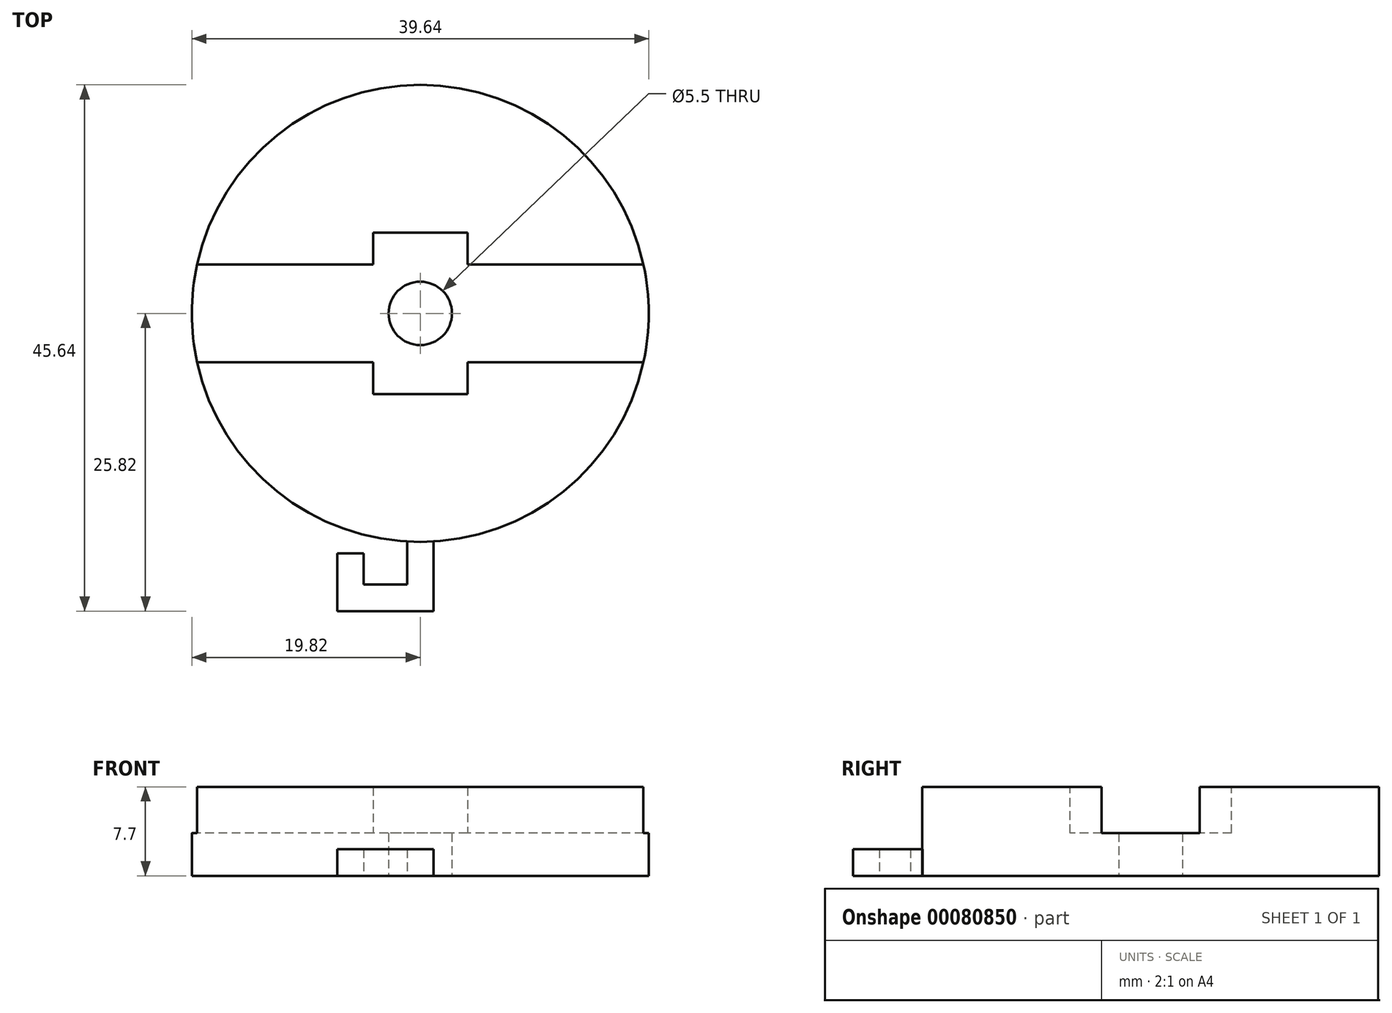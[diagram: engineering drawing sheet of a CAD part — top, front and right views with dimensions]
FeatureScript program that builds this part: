
annotation { "Feature Type Name" : "Feature", "Feature Type Description" : "" }
export const myFeature = defineFeature(function(context is Context, id is Id, definition is map)
    precondition{}
    {
        {
            var Q0;
            Q0=qCreatedBy(makeId("Top.planeOp"),FACE);
            var sketch = newSketch(context, id + "F0", { "sketchPlane" : qUnion([Q0])});
            skCircle(sketch, "E0", {"center": v(0, 0) * mm, "radius": 19.82 * mm});
            skSolve(sketch);
        }
        {
            var Q0;
            Q0 = qSketchRegion(id + "F0", true);
            extrude(context, id + "F1", {"entities" : qUnion([Q0]), "depth" : 7.7 * mm});
        }
        {
            var Q0;
            Q0=makeQuery(id+"F1.opExtrude","CAP_FACE",FACE,{"disambiguationData":[OSD([sQuery(id+"F0.wireOp",EDGE,"E0")])],"isStart":false});
            var sketch = newSketch(context, id + "F2", { "sketchPlane" : qUnion([Q0])});
            skLineSegment(sketch, "E1.bottom", {"start": v(4.1, 7) * mm, "end": v(-4.1, 7) * mm});
            skLineSegment(sketch, "E1.top", {"start": v(4.1, -7) * mm, "end": v(-4.1, -7) * mm});
            skLineSegment(sketch, "E1.left", {"start": v(4.1, 7) * mm, "end": v(4.1, -7) * mm});
            skLineSegment(sketch, "E1.right", {"start": v(-4.1, 7) * mm, "end": v(-4.1, -7) * mm});
            skPoint(sketch, "E1.middle", {"position": v(0, 0) * mm});
            skSolve(sketch);
        }
        {
            var Q0;
            Q0 = qSketchRegion(id + "F2", true);
            extrude(context, id + "F3", {"entities" : qUnion([Q0]), "operationType" : NewBodyOperationType.REMOVE, "oppositeDirection" : true, "depth" : 4 * mm});
        }
        {
            var Q0;
            Q0=makeQuery(id+"F1.opExtrude","CAP_FACE",FACE,{"disambiguationData":[OSD([sQuery(id+"F0.wireOp",EDGE,"E0")])],"isStart":false});
            var sketch = newSketch(context, id + "F4", { "sketchPlane" : qUnion([Q0])});
            skLineSegment(sketch, "E2.bottom", {"start": v(20.32, -4.25) * mm, "end": v(-20.32, -4.25) * mm});
            skLineSegment(sketch, "E2.top", {"start": v(20.32, 4.25) * mm, "end": v(-20.32, 4.25) * mm});
            skLineSegment(sketch, "E2.left", {"start": v(20.32, -4.25) * mm, "end": v(20.32, 4.25) * mm});
            skLineSegment(sketch, "E2.right", {"start": v(-20.32, -4.25) * mm, "end": v(-20.32, 4.25) * mm});
            skPoint(sketch, "E2.middle", {"position": v(0, 0) * mm});
            skSolve(sketch);
        }
        {
            var Q0;
            Q0 = qSketchRegion(id + "F4", true);
            extrude(context, id + "F5", {"entities" : qUnion([Q0]), "operationType" : NewBodyOperationType.REMOVE, "oppositeDirection" : true, "depth" : 4 * mm});
        }
        {
            var Q0;
            Q0=makeQuery(id+"F1.opExtrude","CAP_FACE",FACE,{"disambiguationData":[OSD([sQuery(id+"F0.wireOp",EDGE,"E0")])],"isStart":true});
            var sketch = newSketch(context, id + "F6", { "sketchPlane" : qUnion([Q0])});
            skLineSegment(sketch, "E3.bottom", {"start": v(1.15, 25.82) * mm, "end": v(-1.15, 25.82) * mm});
            skLineSegment(sketch, "E3.left", {"start": v(1.15, 19.82) * mm, "end": v(1.15, 25.82) * mm});
            skLineSegment(sketch, "E3.right", {"start": v(-1.15, 19.82) * mm, "end": v(-1.15, 25.82) * mm});
            skPoint(sketch, "E3.middle", {"position": v(0, 22.82) * mm});
            skLineSegment(sketch, "E4.bottom", {"start": v(1.15, 25.82) * mm, "end": v(-7.2, 25.82) * mm});
            skLineSegment(sketch, "E4.top", {"start": v(1.15, 23.52) * mm, "end": v(-7.2, 23.52) * mm});
            skLineSegment(sketch, "E4.left", {"start": v(1.15, 25.82) * mm, "end": v(1.15, 23.52) * mm});
            skLineSegment(sketch, "E4.right", {"start": v(-7.2, 25.82) * mm, "end": v(-7.2, 23.52) * mm});
            skLineSegment(sketch, "E5.bottom", {"start": v(-7.2, 25.82) * mm, "end": v(-4.9, 25.82) * mm});
            skLineSegment(sketch, "E5.top", {"start": v(-7.2, 20.82) * mm, "end": v(-4.9, 20.82) * mm});
            skLineSegment(sketch, "E5.left", {"start": v(-7.2, 25.82) * mm, "end": v(-7.2, 20.82) * mm});
            skLineSegment(sketch, "E5.right", {"start": v(-4.9, 25.82) * mm, "end": v(-4.9, 20.82) * mm});
            skLineSegment(sketch, "E6", {"start": v(-1.15, 19.82) * mm, "end": v(-1.15, 19.52) * mm});
            skLineSegment(sketch, "E7", {"start": v(-1.15, 19.52) * mm, "end": v(1.17, 19.55) * mm});
            skLineSegment(sketch, "E8", {"start": v(1.17, 19.55) * mm, "end": v(1.15, 19.82) * mm});
            skSolve(sketch);
        }
        {
            var Q0;
            Q0 = qSketchRegion(id + "F6", true);
            extrude(context, id + "F7", {"entities" : qUnion([Q0]), "operationType" : NewBodyOperationType.ADD, "oppositeDirection" : true, "depth" : 2.3 * mm});
        }
        {
            var Q0;
            Q0=makeQuery(id+"F7.boolean.opBoolean","MERGE",FACE,{"derivedFrom":[makeQuery(id+"F1.opExtrude","CAP_FACE",FACE,{"disambiguationData":[OSD([sQuery(id+"F0.wireOp",EDGE,"E0")])],"isStart":true}),makeQuery(id+"F7.opExtrude","CAP_FACE",FACE,{"disambiguationData":[OSD([sQuery(id+"F6.wireOp",EDGE,"E3.left"),sQuery(id+"F6.wireOp",EDGE,"E3.right"),sQuery(id+"F6.wireOp",EDGE,"E4.bottom"),sQuery(id+"F6.wireOp",EDGE,"E4.top"),sQuery(id+"F6.wireOp",EDGE,"E4.left"),sQuery(id+"F6.wireOp",EDGE,"E5.bottom"),sQuery(id+"F6.wireOp",EDGE,"E5.top"),sQuery(id+"F6.wireOp",EDGE,"E5.left"),sQuery(id+"F6.wireOp",EDGE,"E5.right"),sQuery(id+"F6.wireOp",EDGE,"E6"),sQuery(id+"F6.wireOp",EDGE,"E7"),sQuery(id+"F6.wireOp",EDGE,"E8")])],"isStart":true})]});
            var sketch = newSketch(context, id + "F8", { "sketchPlane" : qUnion([Q0])});
            skCircle(sketch, "E9", {"center": v(0, 0) * mm, "radius": 2.75 * mm});
            skSolve(sketch);
        }
        {
            var Q0;
            Q0 = qSketchRegion(id + "F8", true);
            extrude(context, id + "F9", {"entities" : qUnion([Q0]), "operationType" : NewBodyOperationType.REMOVE, "oppositeDirection" : true, "depth" : 25 * mm});
        }
    });
